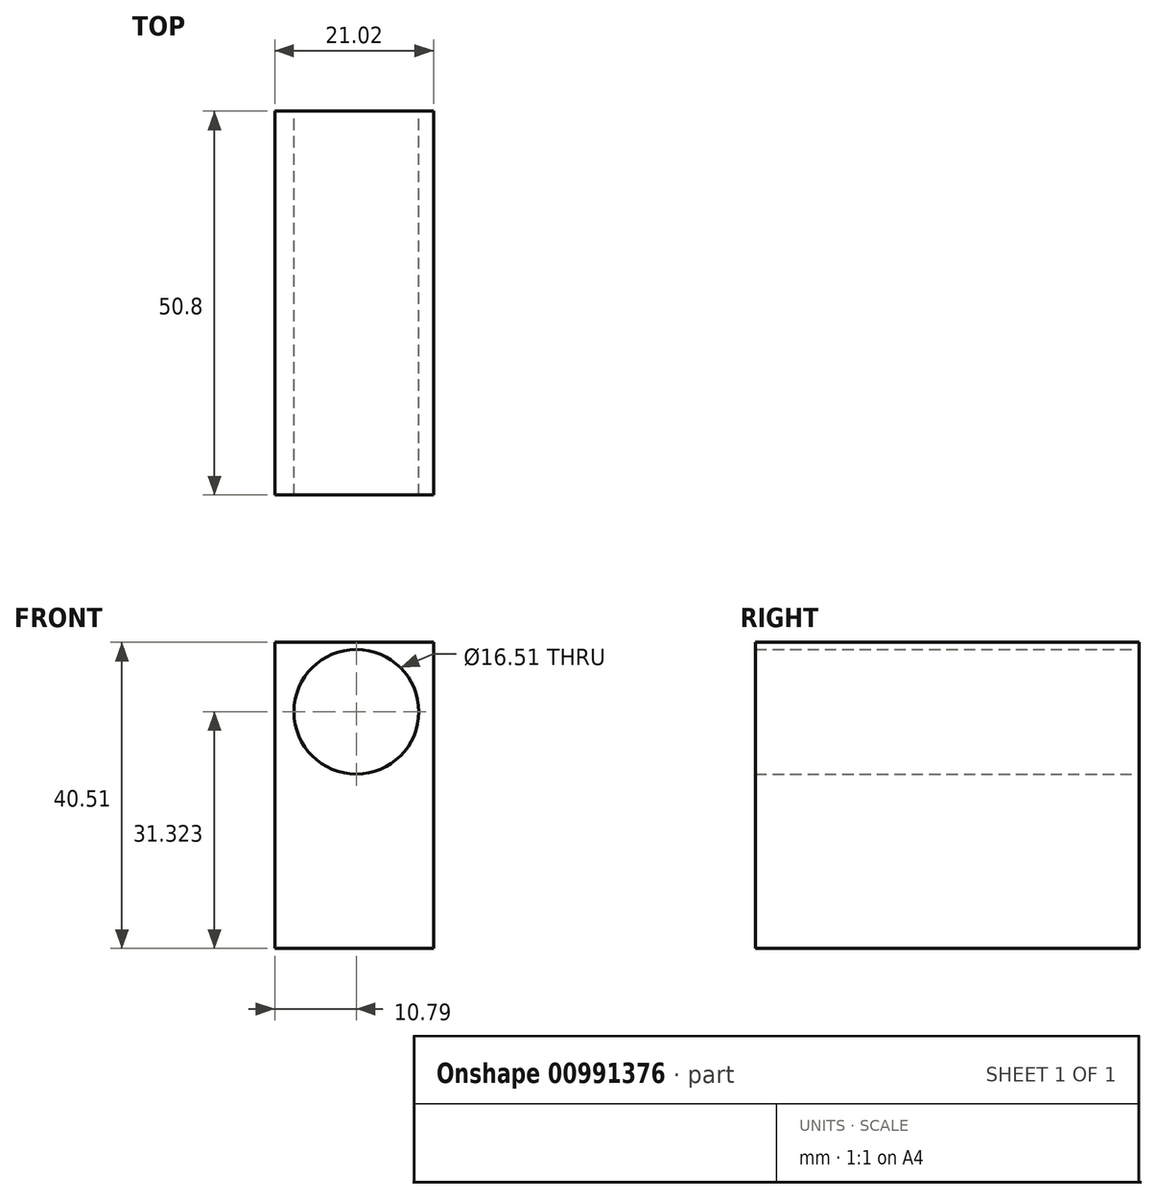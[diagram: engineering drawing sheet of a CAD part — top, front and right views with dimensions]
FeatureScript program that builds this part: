
annotation { "Feature Type Name" : "Feature", "Feature Type Description" : "" }
export const myFeature = defineFeature(function(context is Context, id is Id, definition is map)
    precondition{}
    {
        {
            var Q0;
            Q0=qCreatedBy(makeId("Front.planeOp"),FACE);
            var sketch = newSketch(context, id + "F0", { "sketchPlane" : qUnion([Q0])});
            skLineSegment(sketch, "E0.bottom", {"start": v(-10.79, 22.76) * mm, "end": v(10.23, 22.76) * mm});
            skLineSegment(sketch, "E0.top", {"start": v(-10.79, -17.75) * mm, "end": v(10.23, -17.75) * mm});
            skLineSegment(sketch, "E0.left", {"start": v(-10.79, 22.76) * mm, "end": v(-10.79, -17.75) * mm});
            skLineSegment(sketch, "E0.right", {"start": v(10.23, 22.76) * mm, "end": v(10.23, -17.75) * mm});
            skCircle(sketch, "E1", {"center": v(0, 13.57) * mm, "radius": 8.26 * mm});
            skSolve(sketch);
        }
        {
            var Q0;
            Q0 = qSketchRegion(id + "F0", true);
            extrude(context, id + "F1", {"entities" : qUnion([Q0]), "depth" : 50.8 * mm, "offsetDistance" : 25.4 * mm});
        }
    });
